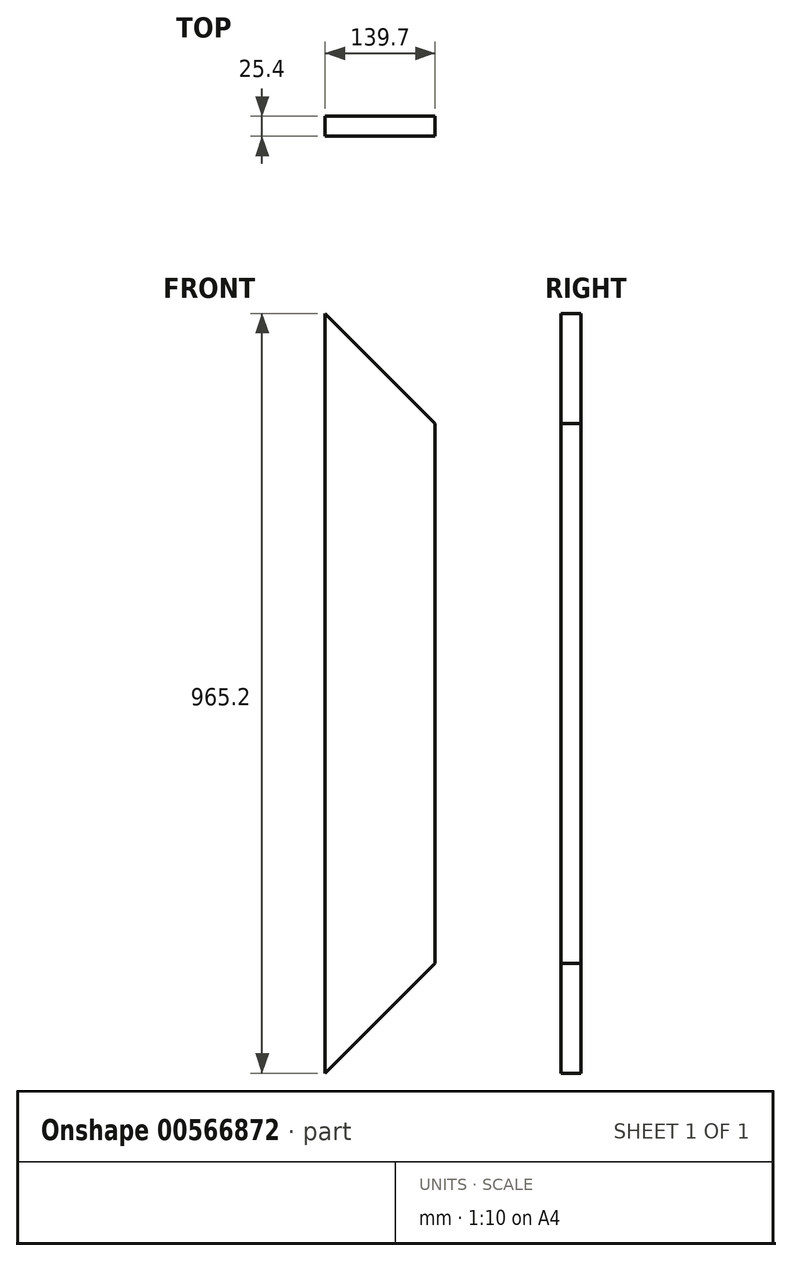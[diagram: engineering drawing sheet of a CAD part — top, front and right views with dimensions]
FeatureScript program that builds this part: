
annotation { "Feature Type Name" : "Feature", "Feature Type Description" : "" }
export const myFeature = defineFeature(function(context is Context, id is Id, definition is map)
    precondition{}
    {
        {
            var Q0;
            Q0=qCreatedBy(makeId("Front.planeOp"),FACE);
            var sketch = newSketch(context, id + "F0", { "sketchPlane" : qUnion([Q0])});
            skLineSegment(sketch, "E0", {"start": v(0, 482.6) * mm, "end": v(0, -482.6) * mm});
            skLineSegment(sketch, "E1", {"start": v(0, -482.6) * mm, "end": v(139.7, -342.9) * mm});
            skLineSegment(sketch, "E2", {"start": v(139.7, -342.9) * mm, "end": v(139.7, 342.9) * mm});
            skLineSegment(sketch, "E3", {"start": v(139.7, 342.9) * mm, "end": v(0, 482.6) * mm});
            skPoint(sketch, "E4", {"position": v(0, 0) * mm});
            skSolve(sketch);
        }
        {
            var Q0;
            Q0=makeQuery(id+"F0.imprint","IMPRINT",FACE,{"disambiguationData":[TD([[makeQuery(id+"F0.imprint","IMPRINT",EDGE,{"derivedFrom":sQuery(id+"F0.wireOp",EDGE,"E0")}),1.0]])]});
            extrude(context, id + "F1", {"entities" : qUnion([Q0]), "depth" : 25.4 * mm, "offsetDistance" : 25.4 * mm});
        }
    });
